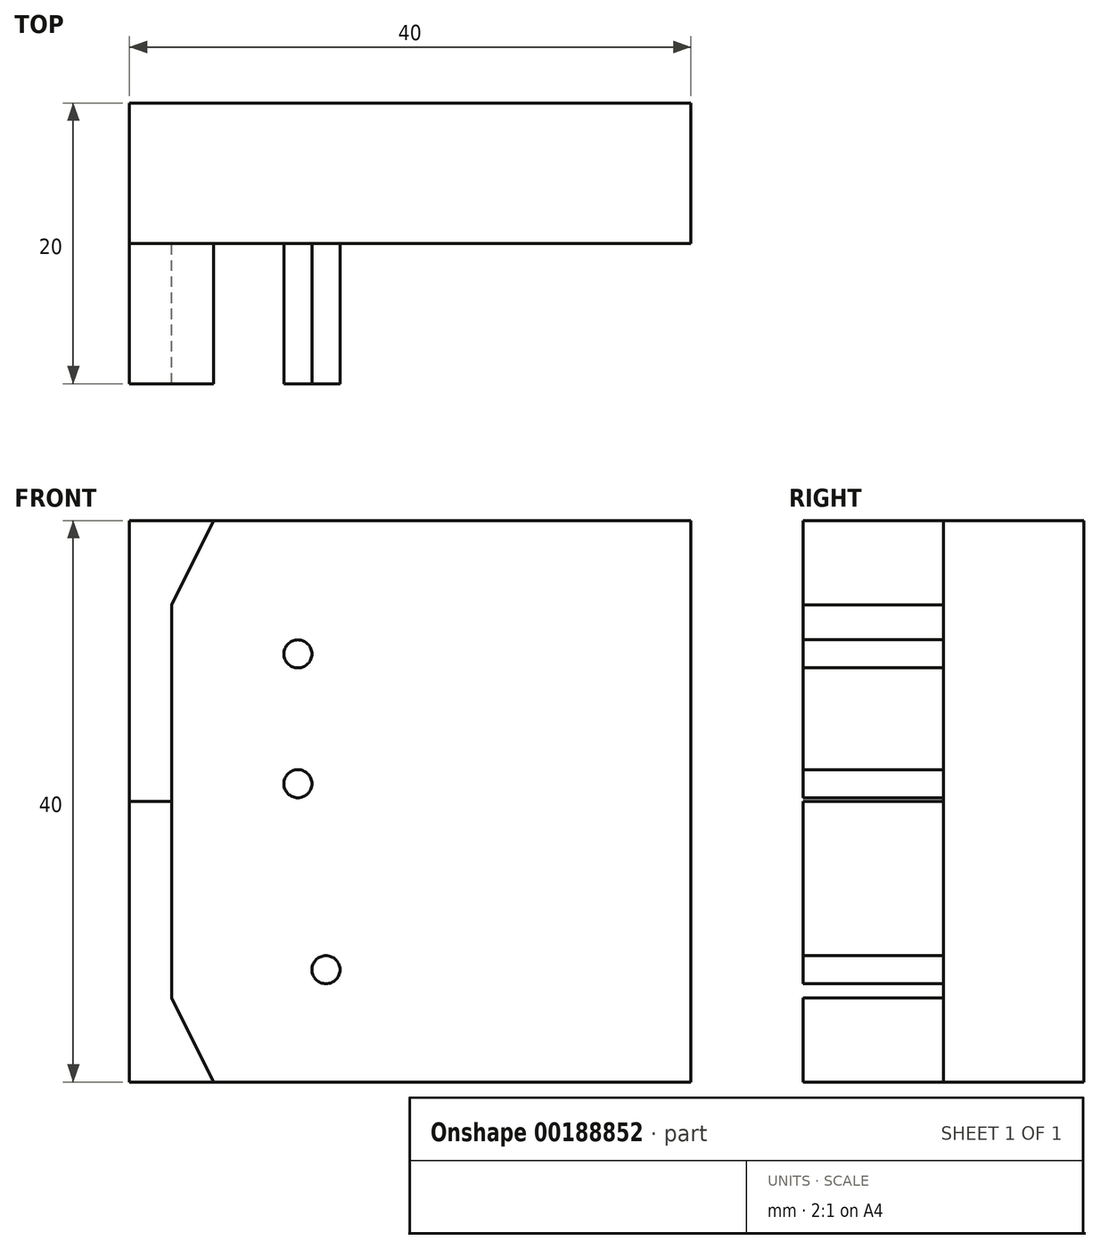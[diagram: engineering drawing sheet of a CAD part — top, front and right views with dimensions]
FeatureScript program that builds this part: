
annotation { "Feature Type Name" : "Feature", "Feature Type Description" : "" }
export const myFeature = defineFeature(function(context is Context, id is Id, definition is map)
    precondition{}
    {
        {
            var Q0;
            Q0=qCreatedBy(makeId("Right.planeOp"),FACE);
            var sketch = newSketch(context, id + "F0", { "sketchPlane" : qUnion([Q0])});
            skLineSegment(sketch, "E0.bottom", {"start": v(5, 20) * mm, "end": v(-5, 20) * mm});
            skLineSegment(sketch, "E0.top", {"start": v(5, -20) * mm, "end": v(-5, -20) * mm});
            skLineSegment(sketch, "E0.left", {"start": v(5, 20) * mm, "end": v(5, -20) * mm});
            skLineSegment(sketch, "E0.right", {"start": v(-5, 20) * mm, "end": v(-5, -20) * mm});
            skPoint(sketch, "E0.middle", {"position": v(0, 0) * mm});
            skSolve(sketch);
        }
        {
            var Q0;
            Q0=makeQuery(id+"F0.imprint","IMPRINT",FACE,{"disambiguationData":[TD([[makeQuery(id+"F0.imprint","IMPRINT",EDGE,{"derivedFrom":sQuery(id+"F0.wireOp",EDGE,"E0.bottom")}),1.0]])]});
            extrude(context, id + "F1", {"entities" : qUnion([Q0]), "depth" : 20 * mm, "hasSecondDirection" : true, "secondDirectionOppositeDirection" : true, "secondDirectionDepth" : 20 * mm});
        }
        {
            var Q0;
            Q0=makeQuery(id+"F1.opExtrude","SWEPT_FACE",FACE,{"disambiguationData":[OSD([sQuery(id+"F0.wireOp",EDGE,"E0.right")])]});
            var sketch = newSketch(context, id + "F2", { "sketchPlane" : qUnion([Q0])});
            skCircle(sketch, "E1", {"center": v(-8, 10.5) * mm, "radius": 1 * mm});
            skCircle(sketch, "E2", {"center": v(-8, 1.25) * mm, "radius": 1 * mm});
            skCircle(sketch, "E3", {"center": v(-6, -12) * mm, "radius": 1 * mm});
            skLineSegment(sketch, "E4", {"start": v(-14, -20) * mm, "end": v(-17, -14) * mm});
            skLineSegment(sketch, "E5", {"start": v(-17, -14) * mm, "end": v(-17, 0) * mm});
            skLineSegment(sketch, "E6", {"start": v(-17, 0) * mm, "end": v(-20, 0) * mm});
            skLineSegment(sketch, "E7", {"start": v(-20, 0) * mm, "end": v(-20, -20) * mm});
            skLineSegment(sketch, "E8", {"start": v(-20, -20) * mm, "end": v(-14, -20) * mm});
            skSolve(sketch);
        }
        {
            var Q0;
            Q0 = qSketchRegion(id + "F2", true);
            extrude(context, id + "F3", {"entities" : qUnion([Q0]), "depth" : 10 * mm});
        }
        {
            var Q0;
            Q0=makeQuery(id+"F3.opExtrude","SWEPT_BODY",BODY,{"disambiguationData":[OSD([sQuery(id+"F2.wireOp",EDGE,"E4"),sQuery(id+"F2.wireOp",EDGE,"E5"),sQuery(id+"F2.wireOp",EDGE,"E6"),sQuery(id+"F2.wireOp",EDGE,"E7"),sQuery(id+"F2.wireOp",EDGE,"E8")])]});
            var Q1;
            Q1=makeQuery(id+"F3.opExtrude","SWEPT_FACE",FACE,{"disambiguationData":[OSD([sQuery(id+"F2.wireOp",EDGE,"E6")])]});
            mirror(context, id + "F4", {"entities" : qUnion([Q0]), "mirrorPlane" : qUnion([Q1])});
        }
    });
